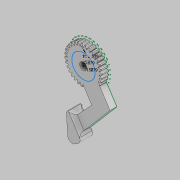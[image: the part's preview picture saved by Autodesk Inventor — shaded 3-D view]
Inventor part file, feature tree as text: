
AUTODESK INVENTOR PART (.ipt)
format: ipt  version: 2021 (Build 250183000, 183)  size: 960,000 bytes
history: native  units: in
note: dims shown in document units (in); Inventor stores cm internally (conversion verified against a paired STEP export)
features: sketch x17, extrude x16, projected_geometry x4, fillet x2, pattern_circular x1
ambient origin geometry x8: Origin, YZ Plane, XZ Plane, XY Plane, X Axis, Y Axis, Z Axis, Center Point
bodies: Solid1 (feature_tree)
feature tree (40):
  sketch  "Sketch1"  dims[d0=1.0in d1=1.0in d2=0.0in]
  extrude  "Extrusion1"  Depth=1.0in TaperAngle=0.0deg
  sketch  "Sketch3"  dims[d5=0.1575in d6=1.0in d7=0.0in]
  extrude  "Extrusion2"  Depth=0.1969in
  extrude  "Extrusion3"  Depth=1.0in TaperAngle=0.0deg
  extrude  "Extrusion4"  Depth=0.5059in
  extrude  "Extrusion5"  Depth=0.189in
  sketch  "Sketch5"  dims[d10=0.5315in d11=0.189in]
  extrude  "Extrusion6"  Depth=0.2067in
  extrude  "Extrusion8"  Depth=1.0in TaperAngle=0.0deg
  extrude  "Extrusion12"  Depth=0.75in TaperAngle=0.0deg
  extrude  "Extrusion13"  Depth=0.75in TaperAngle=0.0deg
  sketch  "Sketch14"  dims[d18=0.5in d19=0.0in d20=0.75in d21=0.0in]
  sketch  "Sketch15"  dims[d25=0.475in d26=0.75in d27=0.0in]
  extrude  "Extrusion18"  Depth=1.0in TaperAngle=0.0deg
  extrude  "Extrusion19"  Depth=0.35in
  fillet  "Fillet4"  Radius=0.35in
  sketch  "Sketch26"  dims[d65=0.25in d66=0.25in]
  sketch  "Sketch27"  dims[d67=0.825in d68=0.6977in]
  extrude  "Extrusion20"  Depth=0.25in
  extrude  "Extrusion22"  Depth=0.6977in
  extrude  "Extrusion23"  Depth=1.0in TaperAngle=0.0deg
  extrude  "Extrusion24"  Depth=0.35in
  fillet  "Fillet7"  Radius=0.1251in
  extrude  "Extrusion25"  Depth=0.125in
  sketch  "Sketch2"  dims[d3=0.8in d4=0.1969in]
  sketch  "Sketch4"  dims[d8=0.5028in d9=0.5059in]
  sketch  "Sketch7"  dims[d12=0.0in d13=0.0in d14=0.2067in]
  sketch  "Sketch13"  dims[d15=0.2283in d16=1.0in d17=0.0in]
  projected_geometry  "Projected Loop2"
  sketch  "Sketch24"  dims[d35=0.185in d36=0.0in d37=1.0in d38=0.0in]
  sketch  "Sketch25"  dims[d62=1.0in d63=1.25in d64=0.35in]
  projected_geometry  "Projected Loop6"
  projected_geometry  "Projected Loop7"
  sketch  "Sketch28"  dims[d69=0.18in d70=1.0in d71=0.0in]
  projected_geometry  "Projected Loop8"
  sketch  "Sketch29"  dims[d72=0.7in d74=0.35in d75=0.1251in d76=0.0in]
  sketch  "Sketch30"  dims[d77=0.125in d78=0.0787in]
  sketch  "Sketch31"  dims[d79=0.0787in d80=0.0787in d81=0.1575in d82=0.1575in d83=0.1251in d84=0.0in d87=0.0in d88=0.0in d89=0.1251in d90=0.0in d92=0.1251in d93=0.0in d95=0.125in d96=0.1969in d97=0.0in d98=0.0in d39=0.5in d40=1.9685in d53=0.5in d54=1.9685in d55=0.5in d56=1.9685in]
  pattern_circular  "CirPattern1"
